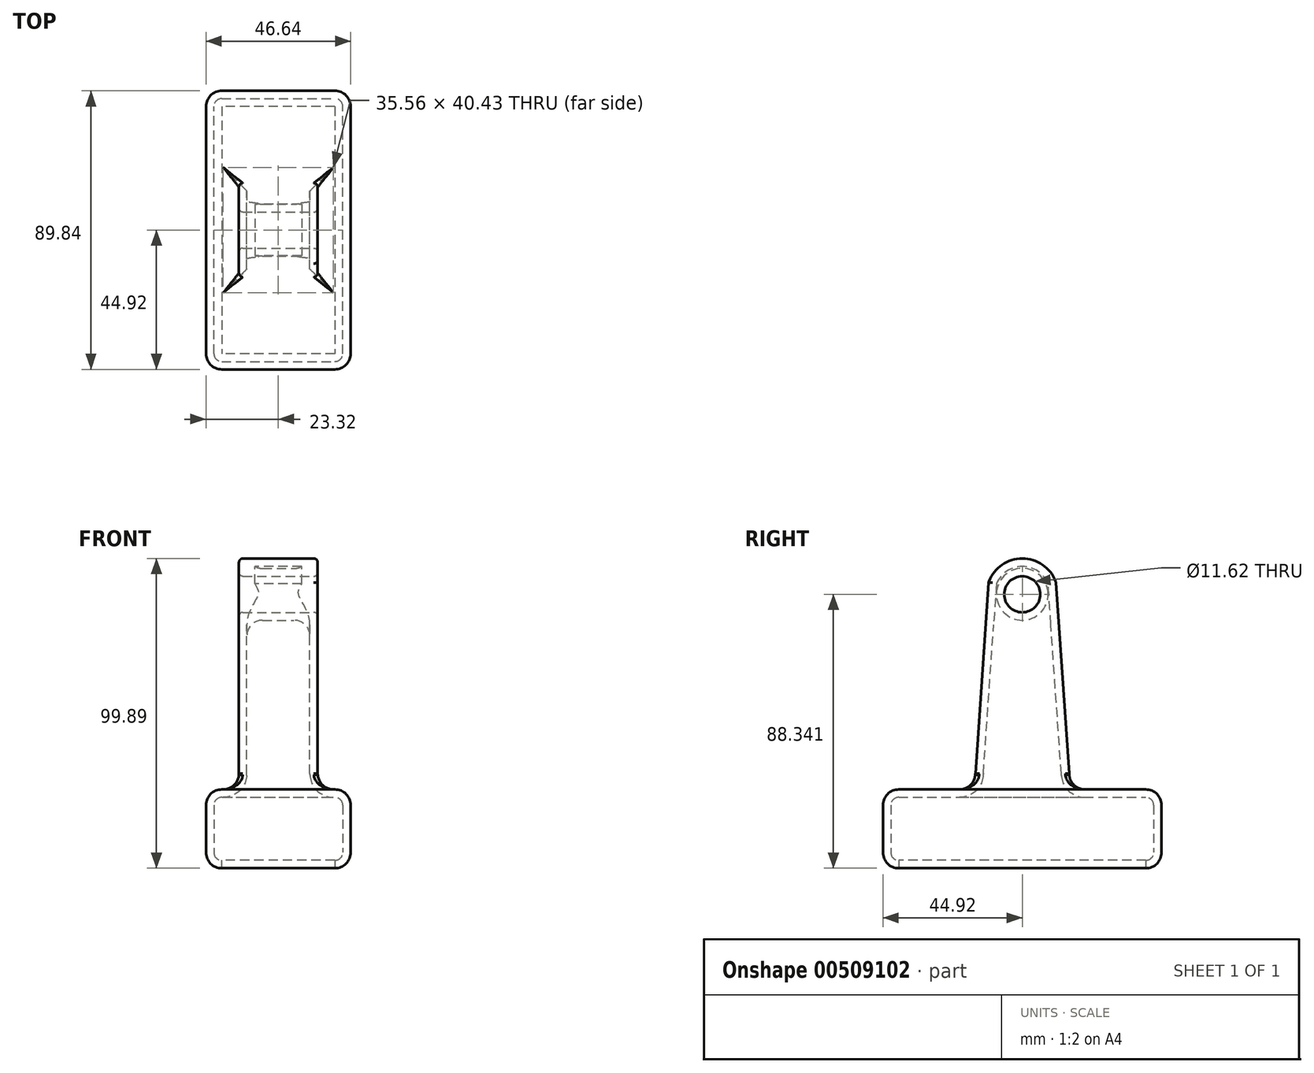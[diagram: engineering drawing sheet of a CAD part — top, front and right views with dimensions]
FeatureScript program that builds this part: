
annotation { "Feature Type Name" : "Feature", "Feature Type Description" : "" }
export const myFeature = defineFeature(function(context is Context, id is Id, definition is map)
    precondition{}
    {
        {
            var Q0;
            Q0=qCreatedBy(makeId("Top.planeOp"),FACE);
            var sketch = newSketch(context, id + "F0", { "sketchPlane" : qUnion([Q0])});
            skLineSegment(sketch, "E0.bottom", {"start": v(23.32, 44.92) * mm, "end": v(-23.32, 44.92) * mm});
            skLineSegment(sketch, "E0.top", {"start": v(23.32, -44.92) * mm, "end": v(-23.32, -44.92) * mm});
            skLineSegment(sketch, "E0.left", {"start": v(23.32, 44.92) * mm, "end": v(23.32, -44.92) * mm});
            skLineSegment(sketch, "E0.right", {"start": v(-23.32, 44.92) * mm, "end": v(-23.32, -44.92) * mm});
            skPoint(sketch, "E0.middle", {"position": v(0, 0) * mm});
            skSolve(sketch);
        }
        {
            var Q0;
            Q0 = qSketchRegion(id + "F0", true);
            extrude(context, id + "F1", {"entities" : qUnion([Q0]), "depth" : 25.4 * mm});
        }
        {
            var Q0;
            Q0=qCreatedBy(makeId("Right.planeOp"),FACE);
            var sketch = newSketch(context, id + "F2", { "sketchPlane" : qUnion([Q0])});
            skLineSegment(sketch, "E1", {"start": v(0, 0) * mm, "end": v(-17.24, 0) * mm});
            skLineSegment(sketch, "E2", {"start": v(-17.24, 0) * mm, "end": v(-10.83, 92.36) * mm});
            skArc(sketch, "E3", {"start": v(0, 99.89) * mm, "mid": v(-6.6, 97.82) * mm, "end": v(-10.83, 92.36) * mm});
            skLineSegment(sketch, "E4", {"start": v(0, 99.89) * mm, "end": v(0, 0) * mm, "construction": true});
            skArc(sketch, "E5.MirrorCS", {"start": v(0, 99.89) * mm, "mid": v(6.6, 97.82) * mm, "end": v(10.83, 92.36) * mm});
            skLineSegment(sketch, "E6.MirrorCS", {"start": v(17.24, 0) * mm, "end": v(10.83, 92.36) * mm});
            skLineSegment(sketch, "E7.MirrorCS", {"start": v(0, 0) * mm, "end": v(17.24, 0) * mm});
            skSolve(sketch);
        }
        {
            var Q0;
            Q0 = qSketchRegion(id + "F2", true);
            extrude(context, id + "F3", {"entities" : qUnion([Q0]), "operationType" : NewBodyOperationType.ADD, "endBound" : BoundingType.SYMMETRIC, "depth" : 25.4 * mm});
        }
        {
            var Q0;
            Q0=makeQuery(id+"F3.opExtrude","CAP_FACE",FACE,{"disambiguationData":[OSD([sQuery(id+"F2.wireOp",EDGE,"E1"),sQuery(id+"F2.wireOp",EDGE,"E2"),sQuery(id+"F2.wireOp",EDGE,"E3"),sQuery(id+"F2.wireOp",EDGE,"E5.MirrorCS"),sQuery(id+"F2.wireOp",EDGE,"E6.MirrorCS"),sQuery(id+"F2.wireOp",EDGE,"E7.MirrorCS")])],"isStart":false});
            var sketch = newSketch(context, id + "F4", { "sketchPlane" : qUnion([Q0])});
            skCircle(sketch, "E8", {"center": v(0, 88.34) * mm, "radius": 5.81 * mm});
            skSolve(sketch);
        }
        {
            var Q0;
            Q0 = qSketchRegion(id + "F4", true);
            extrude(context, id + "F5", {"entities" : qUnion([Q0]), "operationType" : NewBodyOperationType.REMOVE, "oppositeDirection" : true, "depth" : 32.77 * mm});
        }
        {
            var Q0;
            Q0=makeQuery(id+"F1.opExtrude","CAP_FACE",FACE,{"disambiguationData":[OSD([sQuery(id+"F0.wireOp",EDGE,"E0.bottom"),sQuery(id+"F0.wireOp",EDGE,"E0.top"),sQuery(id+"F0.wireOp",EDGE,"E0.left"),sQuery(id+"F0.wireOp",EDGE,"E0.right")])],"isStart":false});
            fillet(context, id + "F6", {"entities" : qUnion([Q0]), "radius" : 5.08 * mm, "tangentPropagation" : true, "allowEdgeOverflow" : false});
        }
        {
            var Q0;
            Q0=makeQuery(id+"F1.opExtrude","CAP_FACE",FACE,{"disambiguationData":[OSD([sQuery(id+"F0.wireOp",EDGE,"E0.bottom"),sQuery(id+"F0.wireOp",EDGE,"E0.top"),sQuery(id+"F0.wireOp",EDGE,"E0.left"),sQuery(id+"F0.wireOp",EDGE,"E0.right")])],"isStart":true});
            var Q1;
            Q1=makeQuery(id+"F1.opExtrude","SWEPT_FACE",FACE,{"disambiguationData":[OSD([sQuery(id+"F0.wireOp",EDGE,"E0.right")])]});
            var Q2;
            Q2=makeQuery(id+"F1.opExtrude","SWEPT_FACE",FACE,{"disambiguationData":[OSD([sQuery(id+"F0.wireOp",EDGE,"E0.top")])]});
            var Q3;
            Q3=makeQuery(id+"F1.opExtrude","SWEPT_FACE",FACE,{"disambiguationData":[OSD([sQuery(id+"F0.wireOp",EDGE,"E0.left")])]});
            fillet(context, id + "F7", {"entities" : qUnion([Q0, Q1, Q2, Q3]), "radius" : 5.08 * mm, "tangentPropagation" : true, "allowEdgeOverflow" : false});
        }
        {
            var Q0;
            Q0=makeQuery(id+"F1.opExtrude","CAP_FACE",FACE,{"disambiguationData":[OSD([sQuery(id+"F0.wireOp",EDGE,"E0.bottom"),sQuery(id+"F0.wireOp",EDGE,"E0.top"),sQuery(id+"F0.wireOp",EDGE,"E0.left"),sQuery(id+"F0.wireOp",EDGE,"E0.right")])],"isStart":true});
            shell(context, id + "F8", {"entities" : qUnion([Q0]), "thickness" : 2.54 * mm});
        }
        {
            var Q0;
            Q0=makeQuery(id+"F3.opExtrude","CAP_FACE",FACE,{"disambiguationData":[OSD([sQuery(id+"F2.wireOp",EDGE,"E1"),sQuery(id+"F2.wireOp",EDGE,"E2"),sQuery(id+"F2.wireOp",EDGE,"E3"),sQuery(id+"F2.wireOp",EDGE,"E5.MirrorCS"),sQuery(id+"F2.wireOp",EDGE,"E6.MirrorCS"),sQuery(id+"F2.wireOp",EDGE,"E7.MirrorCS")])],"isStart":true});
            var Q1;
            Q1=makeQuery(id+"F3.opExtrude","CAP_EDGE",EDGE,{"disambiguationData":[OSD([sQuery(id+"F2.wireOp",EDGE,"E2")])],"isStart":false});
            var Q2;
            Q2=makeQuery(id+"F3.opExtrude","CAP_FACE",FACE,{"disambiguationData":[OSD([sQuery(id+"F2.wireOp",EDGE,"E1"),sQuery(id+"F2.wireOp",EDGE,"E2"),sQuery(id+"F2.wireOp",EDGE,"E3"),sQuery(id+"F2.wireOp",EDGE,"E5.MirrorCS"),sQuery(id+"F2.wireOp",EDGE,"E6.MirrorCS"),sQuery(id+"F2.wireOp",EDGE,"E7.MirrorCS")])],"isStart":false});
            var Q3;
            Q3=makeQuery(id+"F3.opExtrude","SWEPT_FACE",FACE,{"disambiguationData":[OSD([sQuery(id+"F2.wireOp",EDGE,"E2")])]});
            var Q4;
            Q4=makeQuery(id+"F3.opExtrude","SWEPT_EDGE",EDGE,{"disambiguationData":[OSD([sQuery(id+"F2.wireOp",EDGE,"E5.MirrorCS"),sQuery(id+"F2.wireOp",EDGE,"E6.MirrorCS")])]});
            fillet(context, id + "F9", {"entities" : qUnion([Q0, Q1, Q2, Q3, Q4]), "radius" : 1.27 * mm, "tangentPropagation" : true, "allowEdgeOverflow" : false});
        }
        {
            var Q0;
            Q0=makeQuery(id+"F8.opShell","OFFSET_EDGE",EDGE,{"disambiguationData":[OSD([sQuery(id+"F2.wireOp",EDGE,"E1"),sQuery(id+"F2.wireOp",EDGE,"E2"),sQuery(id+"F2.wireOp",EDGE,"E3"),sQuery(id+"F2.wireOp",EDGE,"E5.MirrorCS"),sQuery(id+"F2.wireOp",EDGE,"E6.MirrorCS"),sQuery(id+"F2.wireOp",EDGE,"E7.MirrorCS"),sQuery(id+"F4.wireOp",EDGE,"E8")])]});
            var Q1;
            Q1=makeQuery(id+"F8.opShell","OFFSET_EDGE",EDGE,{"disambiguationData":[OSD([sQuery(id+"F4.wireOp",EDGE,"E8")])]});
            fillet(context, id + "F10", {"entities" : qUnion([Q0, Q1]), "radius" : 5.08 * mm, "tangentPropagation" : true, "allowEdgeOverflow" : false});
        }
    });
